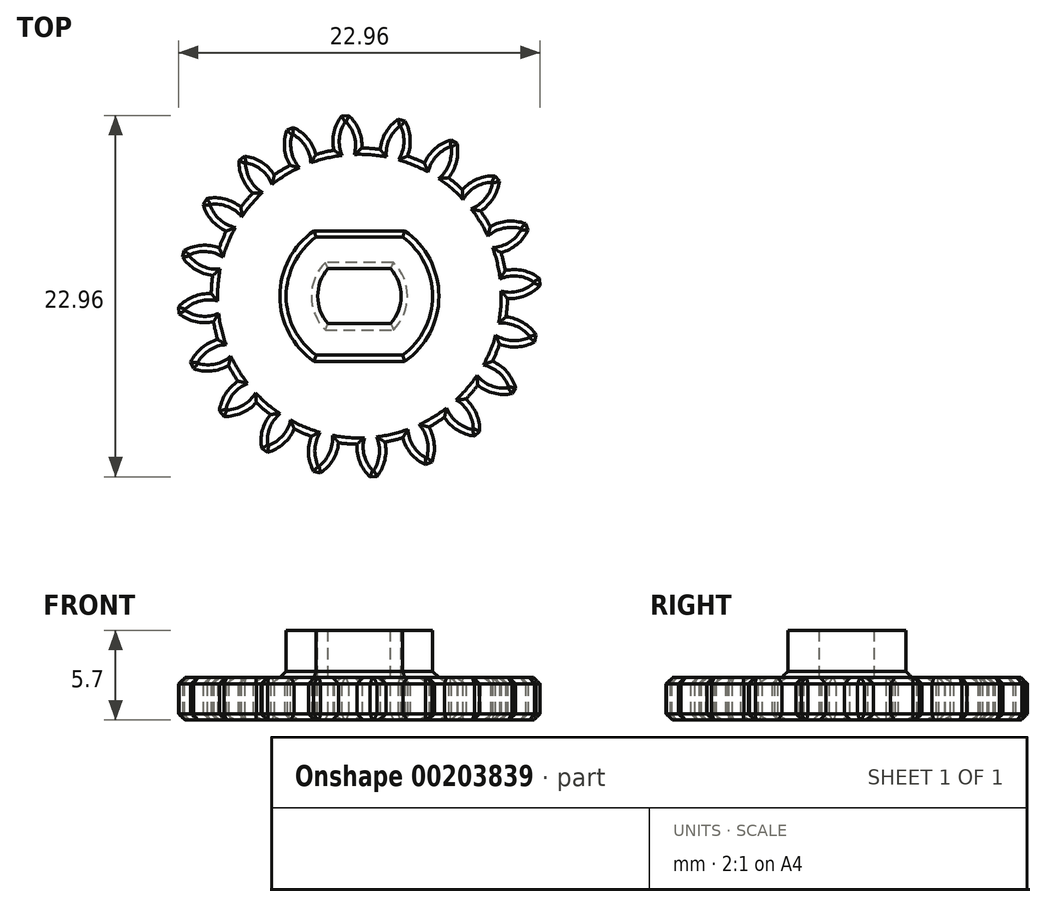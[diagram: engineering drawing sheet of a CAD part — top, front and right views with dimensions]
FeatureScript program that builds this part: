
annotation { "Feature Type Name" : "Feature", "Feature Type Description" : "" }
export const myFeature = defineFeature(function(context is Context, id is Id, definition is map)
    precondition{}
    {
        {
            assignVariable(context, id + "F0", {"name" : "GearDepth", "anyValue" : 4 - 1.3});
        }
        {
            var Q0;
            Q0=qCreatedBy(makeId("Top.planeOp"),FACE);
            var sketch = newSketch(context, id + "F1", { "sketchPlane" : qUnion([Q0])});
            skCircle(sketch, "E0", {"center": v(0, 0) * mm, "radius": 9.4 * mm});
            skCircle(sketch, "E1", {"center": v(0, 0) * mm, "radius": 10.45 * mm, "construction": true});
            skCircle(sketch, "E2", {"center": v(0, 0) * mm, "radius": 11.5 * mm, "construction": true});
            skLineSegment(sketch, "E3", {"start": v(0, 0) * mm, "end": v(0, 17.6) * mm, "construction": true});
            skLineSegment(sketch, "E4", {"start": v(0, 0) * mm, "end": v(-1.42, 18) * mm, "construction": true});
            skLineSegment(sketch, "E5", {"start": v(0, 10.45) * mm, "end": v(-10.54, 10.45) * mm, "construction": true});
            skLineSegment(sketch, "E6", {"start": v(0, 10.45) * mm, "end": v(-10.3, 6.7) * mm, "construction": true});
            skCircle(sketch, "E7", {"center": v(0, 10.45) * mm, "radius": 2.61 * mm, "construction": true});
            skCircle(sketch, "E8", {"center": v(-2.46, 9.56) * mm, "radius": 2.61 * mm, "construction": true});
            skArc(sketch, "E9", {"start": v(-4.91, 10.45) * mm, "mid": v(-4.92, 10.42) * mm, "end": v(-4.94, 10.39) * mm});
            skArc(sketch, "E10.trimOffspring", {"start": v(0.15, 9.4) * mm, "mid": v(-0.03, 10.54) * mm, "end": v(-0.68, 11.48) * mm});
            skArc(sketch, "E11.MirrorCS", {"start": v(-1.62, 9.27) * mm, "mid": v(-1.62, 10.41) * mm, "end": v(-1.12, 11.45) * mm});
            skLineSegment(sketch, "E12", {"start": v(-1.12, 11.45) * mm, "end": v(-0.68, 11.48) * mm});
            skArc(sketch, "E13.1.0", {"start": v(-2.76, 9) * mm, "mid": v(-3.29, 10.01) * mm, "end": v(-4.2, 10.7) * mm});
            skLineSegment(sketch, "E13.1.1", {"start": v(-4.6, 10.54) * mm, "end": v(-4.2, 10.7) * mm});
            skArc(sketch, "E13.1.2", {"start": v(-4.4, 8.31) * mm, "mid": v(-4.76, 9.4) * mm, "end": v(-4.6, 10.54) * mm});
            skArc(sketch, "E13.2.0", {"start": v(-5.4, 7.7) * mm, "mid": v(-6.22, 8.5) * mm, "end": v(-7.3, 8.89) * mm});
            skLineSegment(sketch, "E13.2.1", {"start": v(-7.64, 8.6) * mm, "end": v(-7.3, 8.89) * mm});
            skArc(sketch, "E13.2.2", {"start": v(-6.76, 6.54) * mm, "mid": v(-7.43, 7.47) * mm, "end": v(-7.64, 8.6) * mm});
            skArc(sketch, "E13.3.0", {"start": v(-7.52, 5.65) * mm, "mid": v(-8.54, 6.17) * mm, "end": v(-9.69, 6.2) * mm});
            skLineSegment(sketch, "E13.3.1", {"start": v(-9.92, 5.82) * mm, "end": v(-9.69, 6.2) * mm});
            skArc(sketch, "E13.3.2", {"start": v(-8.45, 4.13) * mm, "mid": v(-9.37, 4.81) * mm, "end": v(-9.92, 5.82) * mm});
            skArc(sketch, "E13.4.0", {"start": v(-8.9, 3.05) * mm, "mid": v(-10.03, 3.23) * mm, "end": v(-11.13, 2.9) * mm});
            skLineSegment(sketch, "E13.4.1", {"start": v(-11.23, 2.47) * mm, "end": v(-11.13, 2.9) * mm});
            skArc(sketch, "E13.4.2", {"start": v(-9.32, 1.32) * mm, "mid": v(-10.4, 1.68) * mm, "end": v(-11.23, 2.47) * mm});
            skArc(sketch, "E13.5.0", {"start": v(-9.4, 0.15) * mm, "mid": v(-10.54, -0.03) * mm, "end": v(-11.48, -0.68) * mm});
            skLineSegment(sketch, "E13.5.1", {"start": v(-11.45, -1.12) * mm, "end": v(-11.48, -0.68) * mm});
            skArc(sketch, "E13.5.2", {"start": v(-9.27, -1.62) * mm, "mid": v(-10.41, -1.62) * mm, "end": v(-11.45, -1.12) * mm});
            skArc(sketch, "E13.6.0", {"start": v(-9, -2.76) * mm, "mid": v(-10.01, -3.29) * mm, "end": v(-10.7, -4.2) * mm});
            skLineSegment(sketch, "E13.6.1", {"start": v(-10.54, -4.6) * mm, "end": v(-10.7, -4.2) * mm});
            skArc(sketch, "E13.6.2", {"start": v(-8.31, -4.4) * mm, "mid": v(-9.4, -4.76) * mm, "end": v(-10.54, -4.6) * mm});
            skArc(sketch, "E13.7.0", {"start": v(-7.7, -5.4) * mm, "mid": v(-8.5, -6.22) * mm, "end": v(-8.89, -7.3) * mm});
            skLineSegment(sketch, "E13.7.1", {"start": v(-8.6, -7.64) * mm, "end": v(-8.89, -7.3) * mm});
            skArc(sketch, "E13.7.2", {"start": v(-6.54, -6.76) * mm, "mid": v(-7.47, -7.43) * mm, "end": v(-8.6, -7.64) * mm});
            skArc(sketch, "E13.8.0", {"start": v(-5.65, -7.52) * mm, "mid": v(-6.17, -8.54) * mm, "end": v(-6.2, -9.69) * mm});
            skLineSegment(sketch, "E13.8.1", {"start": v(-5.82, -9.92) * mm, "end": v(-6.2, -9.69) * mm});
            skArc(sketch, "E13.8.2", {"start": v(-4.13, -8.45) * mm, "mid": v(-4.81, -9.37) * mm, "end": v(-5.82, -9.92) * mm});
            skArc(sketch, "E13.9.0", {"start": v(-3.05, -8.9) * mm, "mid": v(-3.23, -10.03) * mm, "end": v(-2.9, -11.13) * mm});
            skLineSegment(sketch, "E13.9.1", {"start": v(-2.47, -11.23) * mm, "end": v(-2.9, -11.13) * mm});
            skArc(sketch, "E13.9.2", {"start": v(-1.32, -9.32) * mm, "mid": v(-1.68, -10.4) * mm, "end": v(-2.47, -11.23) * mm});
            skArc(sketch, "E13.10.0", {"start": v(-0.15, -9.4) * mm, "mid": v(0.03, -10.54) * mm, "end": v(0.68, -11.48) * mm});
            skLineSegment(sketch, "E13.10.1", {"start": v(1.12, -11.45) * mm, "end": v(0.68, -11.48) * mm});
            skArc(sketch, "E13.10.2", {"start": v(1.62, -9.27) * mm, "mid": v(1.62, -10.41) * mm, "end": v(1.12, -11.45) * mm});
            skArc(sketch, "E13.11.0", {"start": v(2.76, -9) * mm, "mid": v(3.29, -10.01) * mm, "end": v(4.2, -10.7) * mm});
            skLineSegment(sketch, "E13.11.1", {"start": v(4.6, -10.54) * mm, "end": v(4.2, -10.7) * mm});
            skArc(sketch, "E13.11.2", {"start": v(4.4, -8.31) * mm, "mid": v(4.76, -9.4) * mm, "end": v(4.6, -10.54) * mm});
            skArc(sketch, "E13.12.0", {"start": v(5.4, -7.7) * mm, "mid": v(6.22, -8.5) * mm, "end": v(7.3, -8.89) * mm});
            skLineSegment(sketch, "E13.12.1", {"start": v(7.64, -8.6) * mm, "end": v(7.3, -8.89) * mm});
            skArc(sketch, "E13.12.2", {"start": v(6.76, -6.54) * mm, "mid": v(7.43, -7.47) * mm, "end": v(7.64, -8.6) * mm});
            skArc(sketch, "E13.13.0", {"start": v(7.52, -5.65) * mm, "mid": v(8.54, -6.17) * mm, "end": v(9.69, -6.2) * mm});
            skLineSegment(sketch, "E13.13.1", {"start": v(9.92, -5.82) * mm, "end": v(9.69, -6.2) * mm});
            skArc(sketch, "E13.13.2", {"start": v(8.45, -4.13) * mm, "mid": v(9.37, -4.81) * mm, "end": v(9.92, -5.82) * mm});
            skArc(sketch, "E13.14.0", {"start": v(8.9, -3.05) * mm, "mid": v(10.03, -3.23) * mm, "end": v(11.13, -2.9) * mm});
            skLineSegment(sketch, "E13.14.1", {"start": v(11.23, -2.47) * mm, "end": v(11.13, -2.9) * mm});
            skArc(sketch, "E13.14.2", {"start": v(9.32, -1.32) * mm, "mid": v(10.4, -1.68) * mm, "end": v(11.23, -2.47) * mm});
            skArc(sketch, "E13.15.0", {"start": v(9.4, -0.15) * mm, "mid": v(10.54, 0.03) * mm, "end": v(11.48, 0.68) * mm});
            skLineSegment(sketch, "E13.15.1", {"start": v(11.45, 1.12) * mm, "end": v(11.48, 0.68) * mm});
            skArc(sketch, "E13.15.2", {"start": v(9.27, 1.62) * mm, "mid": v(10.41, 1.62) * mm, "end": v(11.45, 1.12) * mm});
            skArc(sketch, "E13.16.0", {"start": v(9, 2.76) * mm, "mid": v(10.01, 3.29) * mm, "end": v(10.7, 4.2) * mm});
            skLineSegment(sketch, "E13.16.1", {"start": v(10.54, 4.6) * mm, "end": v(10.7, 4.2) * mm});
            skArc(sketch, "E13.16.2", {"start": v(8.31, 4.4) * mm, "mid": v(9.4, 4.76) * mm, "end": v(10.54, 4.6) * mm});
            skArc(sketch, "E13.17.0", {"start": v(7.7, 5.4) * mm, "mid": v(8.5, 6.22) * mm, "end": v(8.89, 7.3) * mm});
            skLineSegment(sketch, "E13.17.1", {"start": v(8.6, 7.64) * mm, "end": v(8.89, 7.3) * mm});
            skArc(sketch, "E13.17.2", {"start": v(6.54, 6.76) * mm, "mid": v(7.47, 7.43) * mm, "end": v(8.6, 7.64) * mm});
            skArc(sketch, "E13.18.0", {"start": v(5.65, 7.52) * mm, "mid": v(6.17, 8.54) * mm, "end": v(6.2, 9.69) * mm});
            skLineSegment(sketch, "E13.18.1", {"start": v(5.82, 9.92) * mm, "end": v(6.2, 9.69) * mm});
            skArc(sketch, "E13.18.2", {"start": v(4.13, 8.45) * mm, "mid": v(4.81, 9.37) * mm, "end": v(5.82, 9.92) * mm});
            skArc(sketch, "E13.19.0", {"start": v(3.05, 8.9) * mm, "mid": v(3.23, 10.03) * mm, "end": v(2.9, 11.13) * mm});
            skLineSegment(sketch, "E13.19.1", {"start": v(2.47, 11.23) * mm, "end": v(2.9, 11.13) * mm});
            skArc(sketch, "E13.19.2", {"start": v(1.32, 9.32) * mm, "mid": v(1.68, 10.4) * mm, "end": v(2.47, 11.23) * mm});
            skSolve(sketch);
        }
        {
            var Q0;
            {var subQ0=sQuery(id+"F1.wireOp",EDGE,"E10.trimOffspring");Q0=makeQuery(id+"F1.imprint","IMPRINT",FACE,{"disambiguationData":[TD([[makeQuery(id+"F1.imprint","IMPRINT",EDGE,{"derivedFrom":subQ0}),1.0]])]});}
            var Q1;
            {var subQ0=sQuery(id+"F1.wireOp",EDGE,"E0");var subQ1=makeQuery(id+"F1.imprint","INTERSECT",VERTEX,{"derivedFrom":[subQ0,sQuery(id+"F1.wireOp",EDGE,"E10.trimOffspring")]});Q1=makeQuery(id+"F1.imprint","IMPRINT",FACE,{"disambiguationData":[TD([[makeQuery(id+"F1.imprint","IMPRINT",EDGE,{"disambiguationData":[TD([[subQ1,-1.0]])],"derivedFrom":subQ0}),1.0]])]});}
            var Q2;
            {var subQ0=sQuery(id+"F1.wireOp",EDGE,"E13.1.0");Q2=makeQuery(id+"F1.imprint","IMPRINT",FACE,{"disambiguationData":[TD([[makeQuery(id+"F1.imprint","IMPRINT",EDGE,{"derivedFrom":subQ0}),1.0]])]});}
            var Q3;
            {var subQ0=sQuery(id+"F1.wireOp",EDGE,"E13.2.0");Q3=makeQuery(id+"F1.imprint","IMPRINT",FACE,{"disambiguationData":[TD([[makeQuery(id+"F1.imprint","IMPRINT",EDGE,{"derivedFrom":subQ0}),1.0]])]});}
            var Q4;
            {var subQ0=sQuery(id+"F1.wireOp",EDGE,"E13.3.0");Q4=makeQuery(id+"F1.imprint","IMPRINT",FACE,{"disambiguationData":[TD([[makeQuery(id+"F1.imprint","IMPRINT",EDGE,{"derivedFrom":subQ0}),1.0]])]});}
            var Q5;
            {var subQ0=sQuery(id+"F1.wireOp",EDGE,"E13.4.0");Q5=makeQuery(id+"F1.imprint","IMPRINT",FACE,{"disambiguationData":[TD([[makeQuery(id+"F1.imprint","IMPRINT",EDGE,{"derivedFrom":subQ0}),1.0]])]});}
            var Q6;
            {var subQ0=sQuery(id+"F1.wireOp",EDGE,"E13.5.0");Q6=makeQuery(id+"F1.imprint","IMPRINT",FACE,{"disambiguationData":[TD([[makeQuery(id+"F1.imprint","IMPRINT",EDGE,{"derivedFrom":subQ0}),1.0]])]});}
            var Q7;
            {var subQ0=sQuery(id+"F1.wireOp",EDGE,"E13.6.0");Q7=makeQuery(id+"F1.imprint","IMPRINT",FACE,{"disambiguationData":[TD([[makeQuery(id+"F1.imprint","IMPRINT",EDGE,{"derivedFrom":subQ0}),1.0]])]});}
            var Q8;
            {var subQ0=sQuery(id+"F1.wireOp",EDGE,"E13.7.0");Q8=makeQuery(id+"F1.imprint","IMPRINT",FACE,{"disambiguationData":[TD([[makeQuery(id+"F1.imprint","IMPRINT",EDGE,{"derivedFrom":subQ0}),1.0]])]});}
            var Q9;
            {var subQ0=sQuery(id+"F1.wireOp",EDGE,"E13.8.0");Q9=makeQuery(id+"F1.imprint","IMPRINT",FACE,{"disambiguationData":[TD([[makeQuery(id+"F1.imprint","IMPRINT",EDGE,{"derivedFrom":subQ0}),1.0]])]});}
            var Q10;
            {var subQ0=sQuery(id+"F1.wireOp",EDGE,"E13.9.0");Q10=makeQuery(id+"F1.imprint","IMPRINT",FACE,{"disambiguationData":[TD([[makeQuery(id+"F1.imprint","IMPRINT",EDGE,{"derivedFrom":subQ0}),1.0]])]});}
            var Q11;
            {var subQ0=sQuery(id+"F1.wireOp",EDGE,"E13.10.0");Q11=makeQuery(id+"F1.imprint","IMPRINT",FACE,{"disambiguationData":[TD([[makeQuery(id+"F1.imprint","IMPRINT",EDGE,{"derivedFrom":subQ0}),1.0]])]});}
            var Q12;
            {var subQ0=sQuery(id+"F1.wireOp",EDGE,"E13.11.0");Q12=makeQuery(id+"F1.imprint","IMPRINT",FACE,{"disambiguationData":[TD([[makeQuery(id+"F1.imprint","IMPRINT",EDGE,{"derivedFrom":subQ0}),1.0]])]});}
            var Q13;
            {var subQ0=sQuery(id+"F1.wireOp",EDGE,"E13.12.0");Q13=makeQuery(id+"F1.imprint","IMPRINT",FACE,{"disambiguationData":[TD([[makeQuery(id+"F1.imprint","IMPRINT",EDGE,{"derivedFrom":subQ0}),1.0]])]});}
            var Q14;
            {var subQ0=sQuery(id+"F1.wireOp",EDGE,"E13.13.0");Q14=makeQuery(id+"F1.imprint","IMPRINT",FACE,{"disambiguationData":[TD([[makeQuery(id+"F1.imprint","IMPRINT",EDGE,{"derivedFrom":subQ0}),1.0]])]});}
            var Q15;
            {var subQ0=sQuery(id+"F1.wireOp",EDGE,"E13.14.0");Q15=makeQuery(id+"F1.imprint","IMPRINT",FACE,{"disambiguationData":[TD([[makeQuery(id+"F1.imprint","IMPRINT",EDGE,{"derivedFrom":subQ0}),1.0]])]});}
            var Q16;
            {var subQ0=sQuery(id+"F1.wireOp",EDGE,"E13.15.0");Q16=makeQuery(id+"F1.imprint","IMPRINT",FACE,{"disambiguationData":[TD([[makeQuery(id+"F1.imprint","IMPRINT",EDGE,{"derivedFrom":subQ0}),1.0]])]});}
            var Q17;
            {var subQ0=sQuery(id+"F1.wireOp",EDGE,"E13.16.0");Q17=makeQuery(id+"F1.imprint","IMPRINT",FACE,{"disambiguationData":[TD([[makeQuery(id+"F1.imprint","IMPRINT",EDGE,{"derivedFrom":subQ0}),1.0]])]});}
            var Q18;
            {var subQ0=sQuery(id+"F1.wireOp",EDGE,"E13.17.0");Q18=makeQuery(id+"F1.imprint","IMPRINT",FACE,{"disambiguationData":[TD([[makeQuery(id+"F1.imprint","IMPRINT",EDGE,{"derivedFrom":subQ0}),1.0]])]});}
            var Q19;
            {var subQ0=sQuery(id+"F1.wireOp",EDGE,"E13.18.0");Q19=makeQuery(id+"F1.imprint","IMPRINT",FACE,{"disambiguationData":[TD([[makeQuery(id+"F1.imprint","IMPRINT",EDGE,{"derivedFrom":subQ0}),1.0]])]});}
            var Q20;
            {var subQ0=sQuery(id+"F1.wireOp",EDGE,"E13.19.0");Q20=makeQuery(id+"F1.imprint","IMPRINT",FACE,{"disambiguationData":[TD([[makeQuery(id+"F1.imprint","IMPRINT",EDGE,{"derivedFrom":subQ0}),1.0]])]});}
            var Q21;
            Q21=sQuery(id+"F1.wireOp",EDGE,"E0");
            var Q22;
            Q22=sQuery(id+"F1.wireOp",EDGE,"E10.trimOffspring");
            var Q23;
            Q23=sQuery(id+"F1.wireOp",EDGE,"E12");
            var Q24;
            Q24=sQuery(id+"F1.wireOp",EDGE,"E11.MirrorCS");
            extrude(context, id + "F2", {"entities" : qUnion([Q0, Q1, Q2, Q3, Q4, Q5, Q6, Q7, Q8, Q9, Q10, Q11, Q12, Q13, Q14, Q15, Q16, Q17, Q18, Q19, Q20]), "surfaceEntities" : qUnion([Q21, Q22, Q23, Q24]), "depth" : (getVariable(context, 'GearDepth')) * mm});
        }
        {
            var Q0;
            Q0=makeQuery(id+"F2.opExtrude","CAP_FACE",FACE,{"disambiguationData":[OSD([sQuery(id+"F1.wireOp",EDGE,"E0"),sQuery(id+"F1.wireOp",EDGE,"E10.trimOffspring"),sQuery(id+"F1.wireOp",EDGE,"E11.MirrorCS"),sQuery(id+"F1.wireOp",EDGE,"E12"),sQuery(id+"F1.wireOp",EDGE,"E13.1.0"),sQuery(id+"F1.wireOp",EDGE,"E13.1.1"),sQuery(id+"F1.wireOp",EDGE,"E13.1.2"),sQuery(id+"F1.wireOp",EDGE,"E13.2.0"),sQuery(id+"F1.wireOp",EDGE,"E13.2.1"),sQuery(id+"F1.wireOp",EDGE,"E13.2.2"),sQuery(id+"F1.wireOp",EDGE,"E13.3.0"),sQuery(id+"F1.wireOp",EDGE,"E13.3.1"),sQuery(id+"F1.wireOp",EDGE,"E13.3.2"),sQuery(id+"F1.wireOp",EDGE,"E13.4.0"),sQuery(id+"F1.wireOp",EDGE,"E13.4.1"),sQuery(id+"F1.wireOp",EDGE,"E13.4.2"),sQuery(id+"F1.wireOp",EDGE,"E13.5.0"),sQuery(id+"F1.wireOp",EDGE,"E13.5.1"),sQuery(id+"F1.wireOp",EDGE,"E13.5.2"),sQuery(id+"F1.wireOp",EDGE,"E13.6.0"),sQuery(id+"F1.wireOp",EDGE,"E13.6.1"),sQuery(id+"F1.wireOp",EDGE,"E13.6.2"),sQuery(id+"F1.wireOp",EDGE,"E13.7.0"),sQuery(id+"F1.wireOp",EDGE,"E13.7.1"),sQuery(id+"F1.wireOp",EDGE,"E13.7.2"),sQuery(id+"F1.wireOp",EDGE,"E13.8.0"),sQuery(id+"F1.wireOp",EDGE,"E13.8.1"),sQuery(id+"F1.wireOp",EDGE,"E13.8.2"),sQuery(id+"F1.wireOp",EDGE,"E13.9.0"),sQuery(id+"F1.wireOp",EDGE,"E13.9.1"),sQuery(id+"F1.wireOp",EDGE,"E13.9.2"),sQuery(id+"F1.wireOp",EDGE,"E13.10.0"),sQuery(id+"F1.wireOp",EDGE,"E13.10.1"),sQuery(id+"F1.wireOp",EDGE,"E13.10.2"),sQuery(id+"F1.wireOp",EDGE,"E13.11.0"),sQuery(id+"F1.wireOp",EDGE,"E13.11.1"),sQuery(id+"F1.wireOp",EDGE,"E13.11.2"),sQuery(id+"F1.wireOp",EDGE,"E13.12.0"),sQuery(id+"F1.wireOp",EDGE,"E13.12.1"),sQuery(id+"F1.wireOp",EDGE,"E13.12.2"),sQuery(id+"F1.wireOp",EDGE,"E13.13.0"),sQuery(id+"F1.wireOp",EDGE,"E13.13.1"),sQuery(id+"F1.wireOp",EDGE,"E13.13.2"),sQuery(id+"F1.wireOp",EDGE,"E13.14.0"),sQuery(id+"F1.wireOp",EDGE,"E13.14.1"),sQuery(id+"F1.wireOp",EDGE,"E13.14.2"),sQuery(id+"F1.wireOp",EDGE,"E13.15.0"),sQuery(id+"F1.wireOp",EDGE,"E13.15.1"),sQuery(id+"F1.wireOp",EDGE,"E13.15.2"),sQuery(id+"F1.wireOp",EDGE,"E13.16.0"),sQuery(id+"F1.wireOp",EDGE,"E13.16.1"),sQuery(id+"F1.wireOp",EDGE,"E13.16.2"),sQuery(id+"F1.wireOp",EDGE,"E13.17.0"),sQuery(id+"F1.wireOp",EDGE,"E13.17.1"),sQuery(id+"F1.wireOp",EDGE,"E13.17.2"),sQuery(id+"F1.wireOp",EDGE,"E13.18.0"),sQuery(id+"F1.wireOp",EDGE,"E13.18.1"),sQuery(id+"F1.wireOp",EDGE,"E13.18.2"),sQuery(id+"F1.wireOp",EDGE,"E13.19.0"),sQuery(id+"F1.wireOp",EDGE,"E13.19.1"),sQuery(id+"F1.wireOp",EDGE,"E13.19.2")])],"isStart":false});
            var sketch = newSketch(context, id + "F3", { "sketchPlane" : qUnion([Q0])});
            skLineSegment(sketch, "E14.bottom", {"start": v(1.99, -1.75) * mm, "end": v(-1.99, -1.75) * mm});
            skLineSegment(sketch, "E14.top", {"start": v(1.99, 1.75) * mm, "end": v(-1.99, 1.75) * mm});
            skPoint(sketch, "E14.middle", {"position": v(0, 0) * mm});
            skArc(sketch, "E15", {"start": v(1.99, -1.75) * mm, "mid": v(2.65, 0) * mm, "end": v(1.99, 1.75) * mm});
            skArc(sketch, "E16", {"start": v(-1.99, 1.75) * mm, "mid": v(-2.65, 0) * mm, "end": v(-1.99, -1.75) * mm});
            skLineSegment(sketch, "E17.0", {"start": v(2.75, 3.75) * mm, "end": v(-2.75, 3.75) * mm});
            skArc(sketch, "E17.1", {"start": v(2.75, -3.75) * mm, "mid": v(4.65, 0) * mm, "end": v(2.75, 3.75) * mm});
            skLineSegment(sketch, "E17.2", {"start": v(2.75, -3.75) * mm, "end": v(-2.75, -3.75) * mm});
            skArc(sketch, "E17.3", {"start": v(-2.75, 3.75) * mm, "mid": v(-4.65, 0) * mm, "end": v(-2.75, -3.75) * mm});
            skSolve(sketch);
        }
        {
            var Q0;
            Q0=makeQuery(id+"F3.imprint","IMPRINT",FACE,{"disambiguationData":[TD([[makeQuery(id+"F3.imprint","IMPRINT",EDGE,{"derivedFrom":sQuery(id+"F3.wireOp",EDGE,"E14.bottom")}),-1.0]])]});
            extrude(context, id + "F4", {"entities" : qUnion([Q0]), "operationType" : NewBodyOperationType.REMOVE, "endBound" : BoundingType.UP_TO_NEXT, "oppositeDirection" : true, "depth" : 25 * mm});
        }
        {
            var Q0;
            Q0=makeQuery(id+"F3.imprint","IMPRINT",FACE,{"disambiguationData":[TD([[makeQuery(id+"F3.imprint","IMPRINT",EDGE,{"derivedFrom":sQuery(id+"F3.wireOp",EDGE,"E14.bottom")}),1.0]])]});
            extrude(context, id + "F5", {"entities" : qUnion([Q0]), "operationType" : NewBodyOperationType.ADD, "depth" : 3 * mm});
        }
        {
            var Q0;
            Q0=makeQuery(id+"F2.opExtrude","CAP_FACE",FACE,{"disambiguationData":[OSD([sQuery(id+"F1.wireOp",EDGE,"E0"),sQuery(id+"F1.wireOp",EDGE,"E10.trimOffspring"),sQuery(id+"F1.wireOp",EDGE,"E11.MirrorCS"),sQuery(id+"F1.wireOp",EDGE,"E12"),sQuery(id+"F1.wireOp",EDGE,"E13.1.0"),sQuery(id+"F1.wireOp",EDGE,"E13.1.1"),sQuery(id+"F1.wireOp",EDGE,"E13.1.2"),sQuery(id+"F1.wireOp",EDGE,"E13.2.0"),sQuery(id+"F1.wireOp",EDGE,"E13.2.1"),sQuery(id+"F1.wireOp",EDGE,"E13.2.2"),sQuery(id+"F1.wireOp",EDGE,"E13.3.0"),sQuery(id+"F1.wireOp",EDGE,"E13.3.1"),sQuery(id+"F1.wireOp",EDGE,"E13.3.2"),sQuery(id+"F1.wireOp",EDGE,"E13.4.0"),sQuery(id+"F1.wireOp",EDGE,"E13.4.1"),sQuery(id+"F1.wireOp",EDGE,"E13.4.2"),sQuery(id+"F1.wireOp",EDGE,"E13.5.0"),sQuery(id+"F1.wireOp",EDGE,"E13.5.1"),sQuery(id+"F1.wireOp",EDGE,"E13.5.2"),sQuery(id+"F1.wireOp",EDGE,"E13.6.0"),sQuery(id+"F1.wireOp",EDGE,"E13.6.1"),sQuery(id+"F1.wireOp",EDGE,"E13.6.2"),sQuery(id+"F1.wireOp",EDGE,"E13.7.0"),sQuery(id+"F1.wireOp",EDGE,"E13.7.1"),sQuery(id+"F1.wireOp",EDGE,"E13.7.2"),sQuery(id+"F1.wireOp",EDGE,"E13.8.0"),sQuery(id+"F1.wireOp",EDGE,"E13.8.1"),sQuery(id+"F1.wireOp",EDGE,"E13.8.2"),sQuery(id+"F1.wireOp",EDGE,"E13.9.0"),sQuery(id+"F1.wireOp",EDGE,"E13.9.1"),sQuery(id+"F1.wireOp",EDGE,"E13.9.2"),sQuery(id+"F1.wireOp",EDGE,"E13.10.0"),sQuery(id+"F1.wireOp",EDGE,"E13.10.1"),sQuery(id+"F1.wireOp",EDGE,"E13.10.2"),sQuery(id+"F1.wireOp",EDGE,"E13.11.0"),sQuery(id+"F1.wireOp",EDGE,"E13.11.1"),sQuery(id+"F1.wireOp",EDGE,"E13.11.2"),sQuery(id+"F1.wireOp",EDGE,"E13.12.0"),sQuery(id+"F1.wireOp",EDGE,"E13.12.1"),sQuery(id+"F1.wireOp",EDGE,"E13.12.2"),sQuery(id+"F1.wireOp",EDGE,"E13.13.0"),sQuery(id+"F1.wireOp",EDGE,"E13.13.1"),sQuery(id+"F1.wireOp",EDGE,"E13.13.2"),sQuery(id+"F1.wireOp",EDGE,"E13.14.0"),sQuery(id+"F1.wireOp",EDGE,"E13.14.1"),sQuery(id+"F1.wireOp",EDGE,"E13.14.2"),sQuery(id+"F1.wireOp",EDGE,"E13.15.0"),sQuery(id+"F1.wireOp",EDGE,"E13.15.1"),sQuery(id+"F1.wireOp",EDGE,"E13.15.2"),sQuery(id+"F1.wireOp",EDGE,"E13.16.0"),sQuery(id+"F1.wireOp",EDGE,"E13.16.1"),sQuery(id+"F1.wireOp",EDGE,"E13.16.2"),sQuery(id+"F1.wireOp",EDGE,"E13.17.0"),sQuery(id+"F1.wireOp",EDGE,"E13.17.1"),sQuery(id+"F1.wireOp",EDGE,"E13.17.2"),sQuery(id+"F1.wireOp",EDGE,"E13.18.0"),sQuery(id+"F1.wireOp",EDGE,"E13.18.1"),sQuery(id+"F1.wireOp",EDGE,"E13.18.2"),sQuery(id+"F1.wireOp",EDGE,"E13.19.0"),sQuery(id+"F1.wireOp",EDGE,"E13.19.1"),sQuery(id+"F1.wireOp",EDGE,"E13.19.2")])],"isStart":true});
            var Q1;
            Q1=makeQuery(id+"F2.opExtrude","CAP_FACE",FACE,{"disambiguationData":[OSD([sQuery(id+"F1.wireOp",EDGE,"E0"),sQuery(id+"F1.wireOp",EDGE,"E10.trimOffspring"),sQuery(id+"F1.wireOp",EDGE,"E11.MirrorCS"),sQuery(id+"F1.wireOp",EDGE,"E12"),sQuery(id+"F1.wireOp",EDGE,"E13.1.0"),sQuery(id+"F1.wireOp",EDGE,"E13.1.1"),sQuery(id+"F1.wireOp",EDGE,"E13.1.2"),sQuery(id+"F1.wireOp",EDGE,"E13.2.0"),sQuery(id+"F1.wireOp",EDGE,"E13.2.1"),sQuery(id+"F1.wireOp",EDGE,"E13.2.2"),sQuery(id+"F1.wireOp",EDGE,"E13.3.0"),sQuery(id+"F1.wireOp",EDGE,"E13.3.1"),sQuery(id+"F1.wireOp",EDGE,"E13.3.2"),sQuery(id+"F1.wireOp",EDGE,"E13.4.0"),sQuery(id+"F1.wireOp",EDGE,"E13.4.1"),sQuery(id+"F1.wireOp",EDGE,"E13.4.2"),sQuery(id+"F1.wireOp",EDGE,"E13.5.0"),sQuery(id+"F1.wireOp",EDGE,"E13.5.1"),sQuery(id+"F1.wireOp",EDGE,"E13.5.2"),sQuery(id+"F1.wireOp",EDGE,"E13.6.0"),sQuery(id+"F1.wireOp",EDGE,"E13.6.1"),sQuery(id+"F1.wireOp",EDGE,"E13.6.2"),sQuery(id+"F1.wireOp",EDGE,"E13.7.0"),sQuery(id+"F1.wireOp",EDGE,"E13.7.1"),sQuery(id+"F1.wireOp",EDGE,"E13.7.2"),sQuery(id+"F1.wireOp",EDGE,"E13.8.0"),sQuery(id+"F1.wireOp",EDGE,"E13.8.1"),sQuery(id+"F1.wireOp",EDGE,"E13.8.2"),sQuery(id+"F1.wireOp",EDGE,"E13.9.0"),sQuery(id+"F1.wireOp",EDGE,"E13.9.1"),sQuery(id+"F1.wireOp",EDGE,"E13.9.2"),sQuery(id+"F1.wireOp",EDGE,"E13.10.0"),sQuery(id+"F1.wireOp",EDGE,"E13.10.1"),sQuery(id+"F1.wireOp",EDGE,"E13.10.2"),sQuery(id+"F1.wireOp",EDGE,"E13.11.0"),sQuery(id+"F1.wireOp",EDGE,"E13.11.1"),sQuery(id+"F1.wireOp",EDGE,"E13.11.2"),sQuery(id+"F1.wireOp",EDGE,"E13.12.0"),sQuery(id+"F1.wireOp",EDGE,"E13.12.1"),sQuery(id+"F1.wireOp",EDGE,"E13.12.2"),sQuery(id+"F1.wireOp",EDGE,"E13.13.0"),sQuery(id+"F1.wireOp",EDGE,"E13.13.1"),sQuery(id+"F1.wireOp",EDGE,"E13.13.2"),sQuery(id+"F1.wireOp",EDGE,"E13.14.0"),sQuery(id+"F1.wireOp",EDGE,"E13.14.1"),sQuery(id+"F1.wireOp",EDGE,"E13.14.2"),sQuery(id+"F1.wireOp",EDGE,"E13.15.0"),sQuery(id+"F1.wireOp",EDGE,"E13.15.1"),sQuery(id+"F1.wireOp",EDGE,"E13.15.2"),sQuery(id+"F1.wireOp",EDGE,"E13.16.0"),sQuery(id+"F1.wireOp",EDGE,"E13.16.1"),sQuery(id+"F1.wireOp",EDGE,"E13.16.2"),sQuery(id+"F1.wireOp",EDGE,"E13.17.0"),sQuery(id+"F1.wireOp",EDGE,"E13.17.1"),sQuery(id+"F1.wireOp",EDGE,"E13.17.2"),sQuery(id+"F1.wireOp",EDGE,"E13.18.0"),sQuery(id+"F1.wireOp",EDGE,"E13.18.1"),sQuery(id+"F1.wireOp",EDGE,"E13.18.2"),sQuery(id+"F1.wireOp",EDGE,"E13.19.0"),sQuery(id+"F1.wireOp",EDGE,"E13.19.1"),sQuery(id+"F1.wireOp",EDGE,"E13.19.2")])],"isStart":false});
            chamfer(context, id + "F6", {"entities" : qUnion([Q0, Q1]), "width" : 0.4 * mm, "tangentPropagation" : true});
        }
    });
